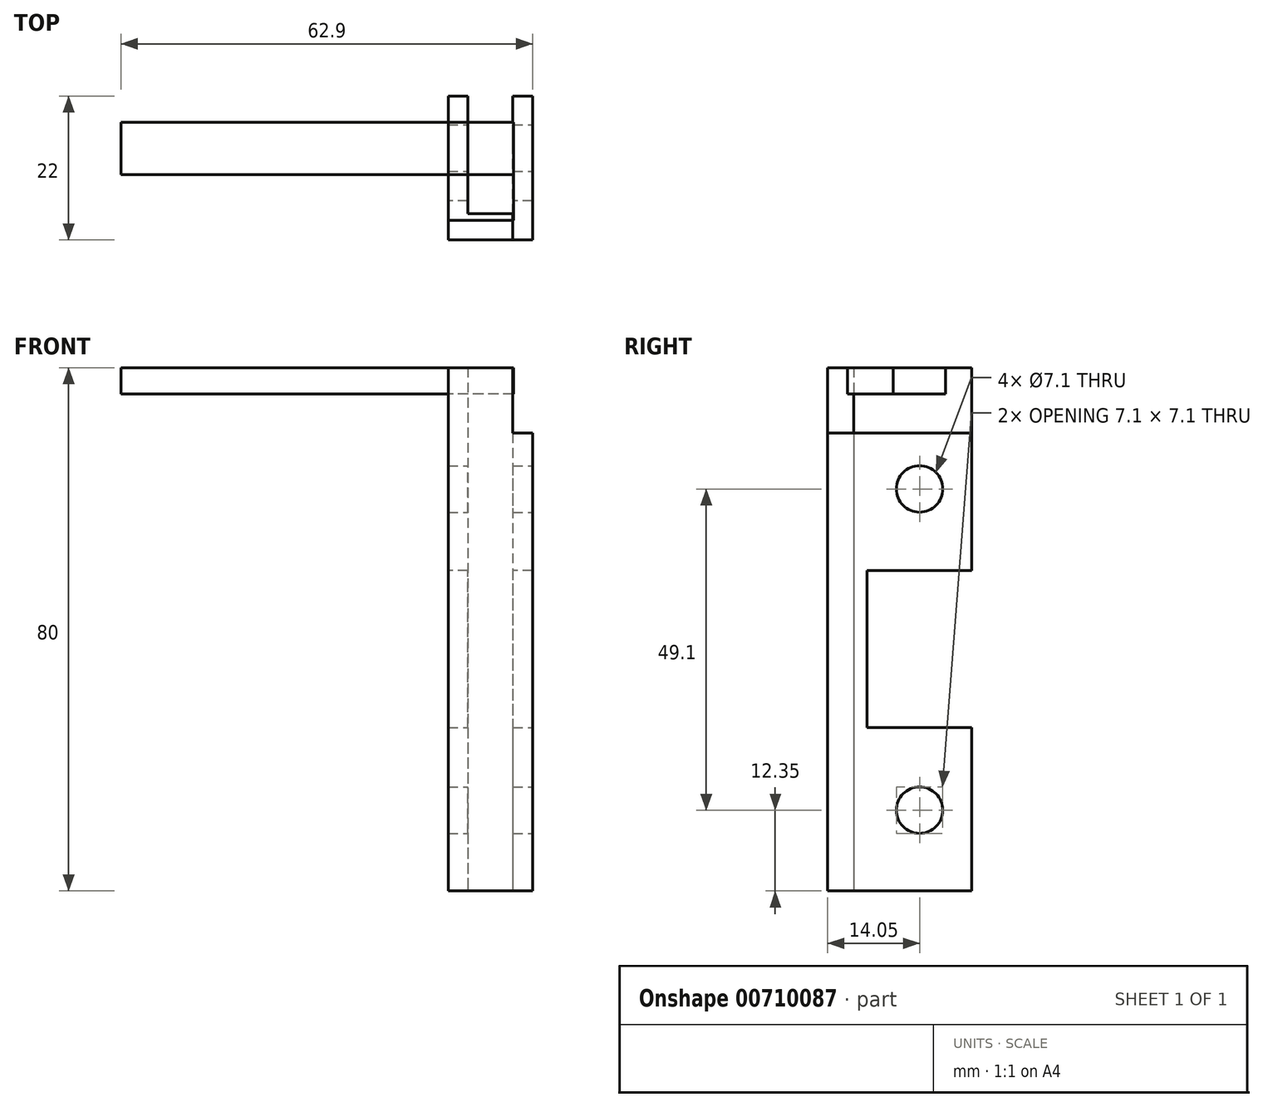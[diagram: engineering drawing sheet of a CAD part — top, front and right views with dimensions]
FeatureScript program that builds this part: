
annotation { "Feature Type Name" : "Feature", "Feature Type Description" : "" }
export const myFeature = defineFeature(function(context is Context, id is Id, definition is map)
    precondition{}
    {
        {
            var Q0;
            Q0=qCreatedBy(makeId("Top.planeOp"),FACE);
            var sketch = newSketch(context, id + "F0", { "sketchPlane" : qUnion([Q0])});
            skLineSegment(sketch, "E0", {"start": v(0, 0) * mm, "end": v(0, 22) * mm});
            skLineSegment(sketch, "E1", {"start": v(0, 22) * mm, "end": v(12.9, 22) * mm});
            skLineSegment(sketch, "E2", {"start": v(12.9, 22) * mm, "end": v(12.9, 0) * mm});
            skLineSegment(sketch, "E3", {"start": v(12.9, 0) * mm, "end": v(0, 0) * mm});
            skLineSegment(sketch, "E4", {"start": v(3, 22) * mm, "end": v(3, 4) * mm});
            skLineSegment(sketch, "E5", {"start": v(3, 4) * mm, "end": v(9.9, 4) * mm});
            skLineSegment(sketch, "E6", {"start": v(9.9, 4) * mm, "end": v(9.9, 22) * mm});
            skSolve(sketch);
        }
        {
            var Q0;
            {var subQ3=sQuery(id+"F0.wireOp",EDGE,"E0");Q0=makeQuery(id+"F0.imprint","IMPRINT",FACE,{"disambiguationData":[TD([[makeQuery(id+"F0.imprint","IMPRINT",EDGE,{"derivedFrom":subQ3}),-1.0]])]});}
            extrude(context, id + "F1", {"entities" : qUnion([Q0]), "depth" : 70 * mm, "offsetDistance" : 25 * mm});
        }
        {
            var Q0;
            Q0=makeQuery(id+"F1.opExtrude","SWEPT_FACE",FACE,{"disambiguationData":[OSD([sQuery(id+"F0.wireOp",EDGE,"E2")])]});
            var sketch = newSketch(context, id + "F2", { "sketchPlane" : qUnion([Q0])});
            skCircle(sketch, "E7", {"center": v(14.05, 61.45) * mm, "radius": 3.55 * mm});
            skCircle(sketch, "E8", {"center": v(14.05, 12.35) * mm, "radius": 3.55 * mm});
            skSolve(sketch);
        }
        {
            var Q0;
            Q0=makeQuery(id+"F2.imprint","IMPRINT",FACE,{"disambiguationData":[TD([[makeQuery(id+"F2.imprint","IMPRINT",EDGE,{"derivedFrom":sQuery(id+"F2.wireOp",EDGE,"E7")}),1.0]])]});
            var Q1;
            Q1=makeQuery(id+"F2.imprint","IMPRINT",FACE,{"disambiguationData":[TD([[makeQuery(id+"F2.imprint","IMPRINT",EDGE,{"derivedFrom":sQuery(id+"F2.wireOp",EDGE,"E8")}),1.0]])]});
            extrude(context, id + "F3", {"entities" : qUnion([Q0, Q1]), "operationType" : NewBodyOperationType.REMOVE, "endBound" : BoundingType.THROUGH_ALL, "oppositeDirection" : true, "depth" : 25 * mm, "offsetDistance" : 25 * mm});
        }
        {
            var Q0;
            Q0=makeQuery(id+"F1.opExtrude","CAP_FACE",FACE,{"disambiguationData":[OSD([sQuery(id+"F0.wireOp",EDGE,"E0"),sQuery(id+"F0.wireOp",EDGE,"E1"),sQuery(id+"F0.wireOp",EDGE,"E2"),sQuery(id+"F0.wireOp",EDGE,"E3"),sQuery(id+"F0.wireOp",EDGE,"E4"),sQuery(id+"F0.wireOp",EDGE,"E5"),sQuery(id+"F0.wireOp",EDGE,"E6")])],"isStart":false});
            var sketch = newSketch(context, id + "F4", { "sketchPlane" : qUnion([Q0])});
            skLineSegment(sketch, "E9", {"start": v(9.9, 4) * mm, "end": v(9.9, 0) * mm});
            skPoint(sketch, "E9.endSnap0", {"position": v(6.45, 0) * mm});
            skSolve(sketch);
        }
        {
            var Q0;
            {var subQ4=sQuery(id+"F4.wireOp",EDGE,"E9");Q0=makeQuery(id+"F4.imprint","IMPRINT",FACE,{"disambiguationData":[TD([[makeQuery(id+"F4.imprint","IMPRINT",EDGE,{"derivedFrom":subQ4}),-1.0]])]});}
            extrude(context, id + "F5", {"entities" : qUnion([Q0]), "operationType" : NewBodyOperationType.ADD, "depth" : 10 * mm, "offsetDistance" : 25 * mm});
        }
        {
            var Q0;
            {var subQ0=sQuery(id+"F0.wireOp",EDGE,"E0");Q0=makeQuery(id+"F5.boolean.opBoolean","MERGE",FACE,{"derivedFrom":[makeQuery(id+"F1.opExtrude","SWEPT_FACE",FACE,{"disambiguationData":[OSD([subQ0])]}),makeQuery(id+"F5.opExtrude","SWEPT_FACE",FACE,{"disambiguationData":[OSD([subQ0])]})]});}
            var sketch = newSketch(context, id + "F6", { "sketchPlane" : qUnion([Q0])});
            skLineSegment(sketch, "E10", {"start": v(-22, 76) * mm, "end": v(0, 76) * mm});
            skLineSegment(sketch, "E11", {"start": v(-18, 76) * mm, "end": v(-18, 80) * mm});
            skLineSegment(sketch, "E12", {"start": v(-18, 80) * mm, "end": v(0, 80) * mm});
            skLineSegment(sketch, "E13", {"start": v(-10, 76) * mm, "end": v(-10, 80) * mm});
            skSolve(sketch);
        }
        {
            var Q0;
            {var subQ4=sQuery(id+"F6.wireOp",EDGE,"E11");Q0=makeQuery(id+"F6.imprint","IMPRINT",FACE,{"disambiguationData":[TD([[makeQuery(id+"F6.imprint","IMPRINT",EDGE,{"derivedFrom":subQ4}),-1.0]])]});}
            extrude(context, id + "F7", {"entities" : qUnion([Q0]), "depth" : 50 * mm, "offsetDistance" : 25 * mm});
        }
        {
            var Q0;
            {var subQ0=sQuery(id+"F0.wireOp",EDGE,"E1");Q0=makeQuery(id+"F1.opExtrude","SWEPT_FACE",FACE,{"disambiguationData":[OSD([subQ0]),TDD([makeQuery(id+"F0.imprint","IMPRINT",EDGE,{"disambiguationData":[TD([[makeQuery(id+"F0.imprint","INTERSECT",VERTEX,{"derivedFrom":[subQ0,sQuery(id+"F0.wireOp",EDGE,"E2")]}),1.0]])],"derivedFrom":subQ0})])]});}
            var sketch = newSketch(context, id + "F8", { "sketchPlane" : qUnion([Q0])});
            skLineSegment(sketch, "E14", {"start": v(-12.9, 49) * mm, "end": v(0, 49) * mm});
            skLineSegment(sketch, "E15", {"start": v(0, 49) * mm, "end": v(0, 25) * mm});
            skLineSegment(sketch, "E16", {"start": v(0, 25) * mm, "end": v(-12.9, 25) * mm});
            skLineSegment(sketch, "E17", {"start": v(-12.9, 25) * mm, "end": v(-12.9, 49) * mm});
            skSolve(sketch);
        }
        {
            var Q0;
            Q0=makeQuery(id+"F8.imprint","IMPRINT",FACE,{"disambiguationData":[TD([[makeQuery(id+"F8.imprint","IMPRINT",EDGE,{"derivedFrom":sQuery(id+"F8.wireOp",EDGE,"vN7vXV1M-gyVh-wu98-0U4N-jEQqpl8zVVec")}),1.0]])]});
            var Q1;
            {var subQ0=sQuery(id+"F8.wireOp",EDGE,"E15");Q1=makeQuery(id+"F8.imprint","IMPRINT",FACE,{"disambiguationData":[TD([[makeQuery(id+"F8.imprint","IMPRINT",EDGE,{"derivedFrom":subQ0}),-1.0]])]});}
            var Q2;
            {var subQ0=sQuery(id+"F8.wireOp",EDGE,"E17");Q2=makeQuery(id+"F8.imprint","IMPRINT",FACE,{"disambiguationData":[TD([[makeQuery(id+"F8.imprint","IMPRINT",EDGE,{"derivedFrom":subQ0}),1.0]])]});}
            extrude(context, id + "F9", {"entities" : qUnion([Q0, Q1, Q2]), "operationType" : NewBodyOperationType.REMOVE, "oppositeDirection" : true, "depth" : 16 * mm, "offsetDistance" : 25 * mm});
        }
        {
            var Q0;
            {var subQ0=sQuery(id+"F6.wireOp",EDGE,"E11");Q0=makeQuery(id+"F6.imprint","IMPRINT",FACE,{"disambiguationData":[TD([[makeQuery(id+"F6.imprint","IMPRINT",EDGE,{"derivedFrom":subQ0}),-1.0]])]});}
            extrude(context, id + "F10", {"entities" : qUnion([Q0]), "oppositeDirection" : true, "depth" : 10 * mm, "offsetDistance" : 25 * mm});
        }
        {
            var Q0;
            Q0=makeQuery(id+"F10.opExtrude","SWEPT_FACE",FACE,{"disambiguationData":[OSD([sQuery(id+"F6.wireOp",EDGE,"E13")])]});
            extrude(context, id + "F11", {"entities" : qUnion([Q0]), "depth" : 7 * mm, "offsetDistance" : 25 * mm});
        }
    });
